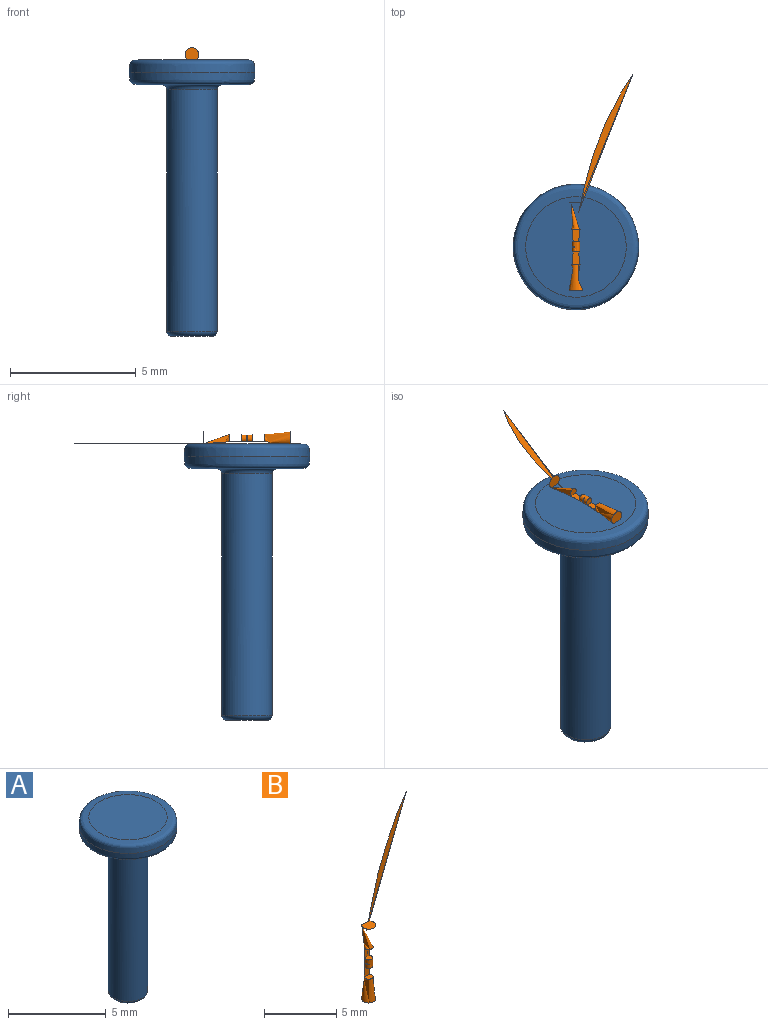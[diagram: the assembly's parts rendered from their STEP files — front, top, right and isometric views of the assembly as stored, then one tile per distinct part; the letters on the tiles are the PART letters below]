
ASSEMBLY  parts=2 mates=1
PART A: 8 faces, bbox 5x5x11 mm
  f0: plane 4.01x4.01mm, normal (0,0,-1), area 8mm2, adj f3,f6
  f1: plane 4.01x4.01mm, normal (0,0,1), area 12.6mm2, adj f2
  f2: bspline ~5x5mm, area 13mm2, adj f1,f3
  f3: bspline ~5x5mm, area 13mm2, adj f0,f2
  f4: cylinder r=1mm len=9.6mm, axis (0,0,1), area 60.3mm2, adj f6,f7
  f5: plane 1.6x1.6mm, normal (0,0,-1), area 2mm2, adj f7
  f6: torus R=1.2mm, axis (0,0,1), area 2.1mm2, adj f0,f4
  f7: torus R=0.8mm, axis (0,0,-1), area 1.8mm2, adj f4,f5
PART B: 14 faces, bbox 8x8x17.3 mm
  f0: torus R=12.35mm, axis (0,0,1), area 3.2mm2, adj f1,f2,f3,f4,f5,f6,f7,f8
  f1: extruded ~0.26x0.02mm, area 0mm2, adj f0,f2,f4
  f2: plane 0.26x0.1mm, normal (0,0,-1), area 0mm2, adj f0,f1
  f3: plane 0.55x0.48mm, normal (0,0,1), area 0.2mm2, adj f0,f13
  f4: plane 0.26x0.1mm, normal (0,0,1), area 0mm2, adj f0,f1
  f5: plane 0.65x0.38mm, normal (0,1,0), area 0.2mm2, adj f0,f6
  f6: plane 0.55x0.48mm, normal (0,0,-1), area 0.2mm2, adj f0,f5
  f7: plane 0.3x0.25mm, normal (0,0,-1), area 0.1mm2, adj f0,f8
  f8: plane 0.5x0.28mm, normal (0,-1,0), area 0.1mm2, adj f0,f7,f9
  f9: plane 0.34x0.27mm, normal (0,0,1), area 0.1mm2, adj f0,f8
  f10: plane 0.5x0.28mm, normal (0,-1,0), area 0.1mm2, adj f0,f11,f12
  f11: plane 0.34x0.27mm, normal (0,0,-1), area 0.1mm2, adj f0,f10
  f12: plane 0.3x0.25mm, normal (0,0,1), area 0.1mm2, adj f0,f10
  f13: plane 6.52x5.64mm, normal (0,1,0), area -14.7mm2, adj f0,f3
PLACE A at identity fixed
PLACE B rot(axis=(-1,0,0),90deg) t=(0,0,0.2)mm
MATE planar B.f5 <-> A.f4  axis (0,0,-1) through (0,-1.75,0)mm
